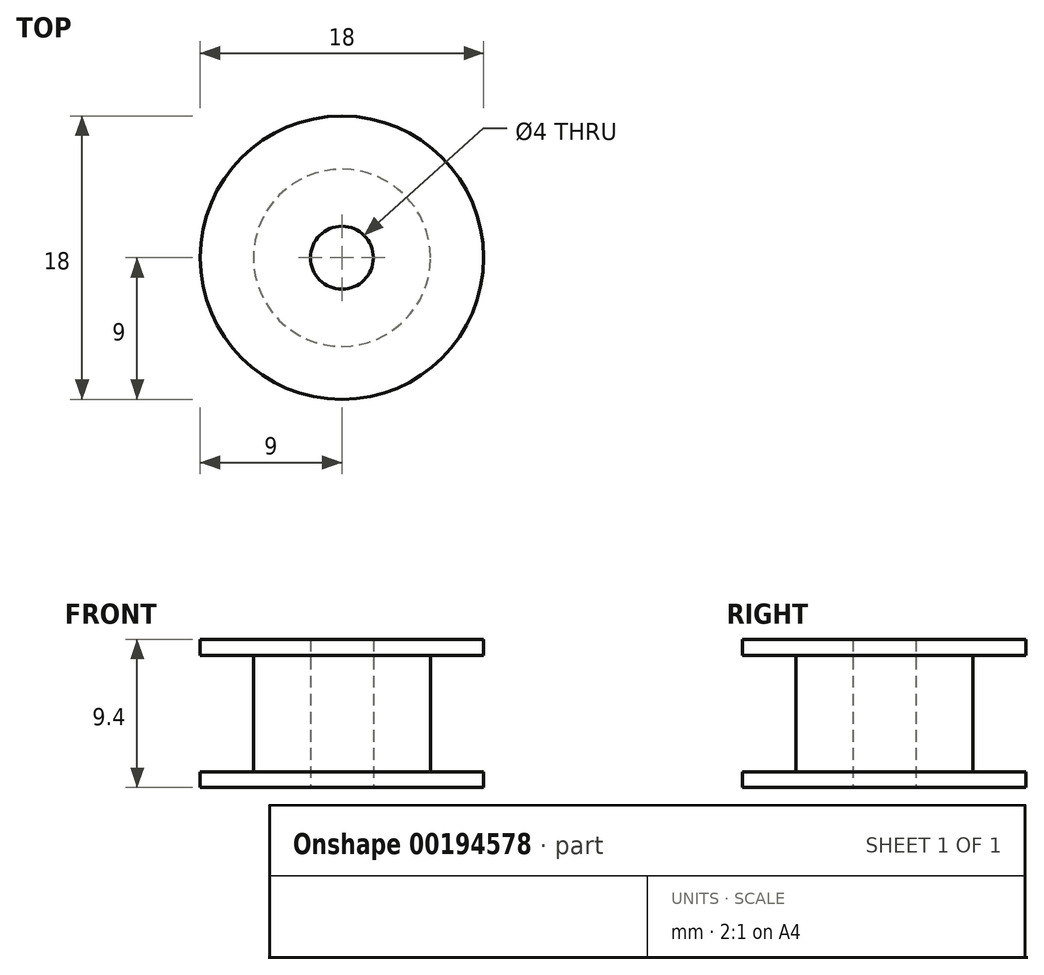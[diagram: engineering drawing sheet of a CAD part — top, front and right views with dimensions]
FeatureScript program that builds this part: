
annotation { "Feature Type Name" : "Feature", "Feature Type Description" : "" }
export const myFeature = defineFeature(function(context is Context, id is Id, definition is map)
    precondition{}
    {
        {
            var Q0;
            Q0=qCreatedBy(makeId("Top.planeOp"),FACE);
            var sketch = newSketch(context, id + "F0", { "sketchPlane" : qUnion([Q0])});
            skCircle(sketch, "E0", {"center": v(0, 0) * mm, "radius": 9 * mm});
            skSolve(sketch);
        }
        {
            var Q0;
            Q0 = qSketchRegion(id + "F0", true);
            extrude(context, id + "F1", {"entities" : qUnion([Q0]), "depth" : 1 * mm});
        }
        {
            var Q0;
            Q0=makeQuery(id+"F1.opExtrude","CAP_FACE",FACE,{"disambiguationData":[OSD([sQuery(id+"F0.wireOp",EDGE,"E0")])],"isStart":false});
            var sketch = newSketch(context, id + "F2", { "sketchPlane" : qUnion([Q0])});
            skCircle(sketch, "E1", {"center": v(0, 0) * mm, "radius": 5.62 * mm});
            skSolve(sketch);
        }
        {
            var Q0;
            Q0 = qSketchRegion(id + "F2", true);
            extrude(context, id + "F3", {"entities" : qUnion([Q0]), "operationType" : NewBodyOperationType.ADD, "depth" : 7.4 * mm});
        }
        {
            var Q0;
            Q0=makeQuery(id+"F3.opExtrude","CAP_FACE",FACE,{"disambiguationData":[OSD([sQuery(id+"F2.wireOp",EDGE,"E1")])],"isStart":false});
            var sketch = newSketch(context, id + "F4", { "sketchPlane" : qUnion([Q0])});
            skCircle(sketch, "E2", {"center": v(0, 0) * mm, "radius": 9 * mm});
            skSolve(sketch);
        }
        {
            var Q0;
            Q0 = qSketchRegion(id + "F4", true);
            extrude(context, id + "F5", {"entities" : qUnion([Q0]), "operationType" : NewBodyOperationType.ADD, "depth" : 1 * mm});
        }
        {
            var Q0;
            Q0=makeQuery(id+"F5.opExtrude","CAP_FACE",FACE,{"disambiguationData":[OSD([sQuery(id+"F4.wireOp",EDGE,"E2")])],"isStart":false});
            var sketch = newSketch(context, id + "F6", { "sketchPlane" : qUnion([Q0])});
            skPoint(sketch, "E3", {"position": v(0, 0) * mm});
            skSolve(sketch);
        }
        {
            var Q0;
            Q0=sQuery(id+"F6.wireOp",VERTEX,"E3");
            var Q1;
            Q1=makeQuery(id+"F1.opExtrude","SWEPT_BODY",BODY,{"disambiguationData":[OSD([sQuery(id+"F0.wireOp",EDGE,"E0")])]});
            hole(context, id + "F7", {"style" : HoleStyle.SIMPLE, "endStyle" : HoleEndStyle.THROUGH, "holeDiameter" : 4 * mm, "locations" : qUnion([Q0]), "scope" : qUnion([Q1]), "isTappedThrough" : true, "startStyle" : HoleStartStyle.PART});
        }
    });
